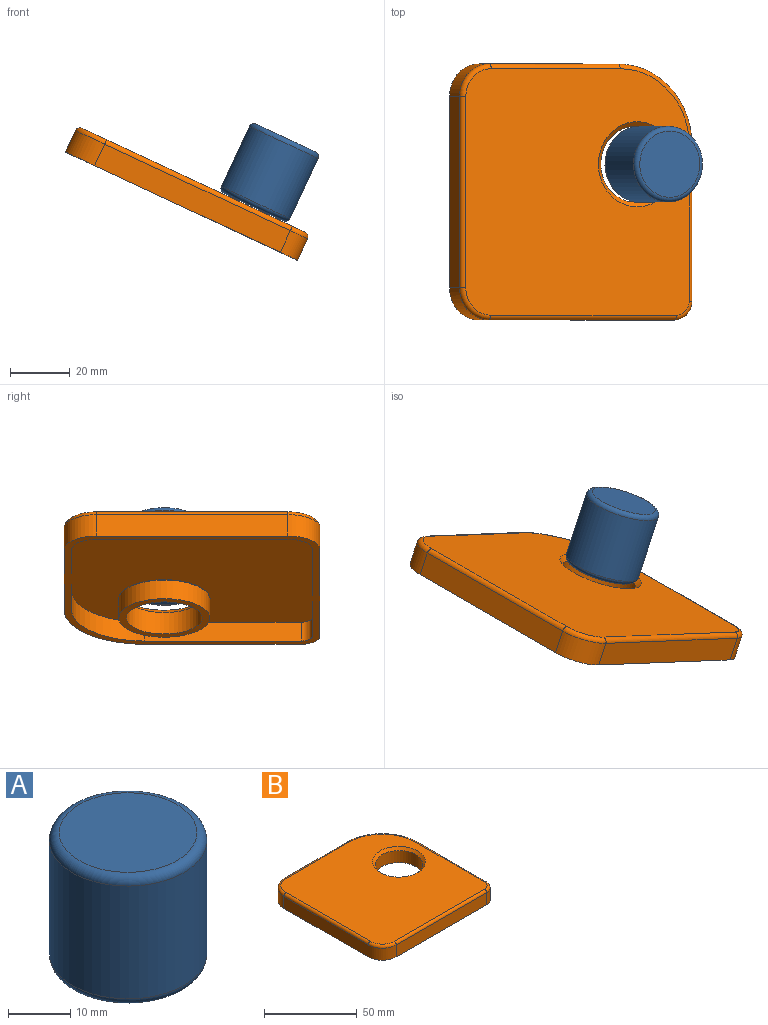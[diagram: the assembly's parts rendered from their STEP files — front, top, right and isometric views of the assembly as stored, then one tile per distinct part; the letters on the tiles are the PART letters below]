
ASSEMBLY  parts=2 mates=1
PART A: 5 faces, bbox 27.4x27.4x25.4 mm
  f0: cylinder r=12.67mm len=25.35mm, axis (0,0,-1), area 1769.9mm2, adj f3,f4
  f1: plane 22.17x22.17mm, normal (0,0,1), area 386.2mm2, adj f4
  f2: plane 22.17x22.17mm, normal (0,0,-1), area 386.2mm2, adj f3
  f3: torus R=11.09mm, axis (0,0,1), area 189.5mm2, adj f0,f2
  f4: torus R=11.09mm, axis (0,0,1), area 189.5mm2, adj f0,f1
PART B: 32 faces, bbox 88.9x88.8x9.5 mm
  f0: plane 30.48x30.48mm, normal (0,0,-1), area 223mm2, adj f11,f30
  f1: plane 85.73x85.73mm, normal (0,0,-1), area 790.6mm2, adj f2,f3,f4,f5,f6,f7,f8,f9
  f2: plane 47.71x7.94mm, normal (0,1,0), area 378.7mm2, adj f1,f3,f9,f14
  f3: cylinder r=10.94mm len=10.94mm, axis (0,0,-1), area 136.4mm2, adj f1,f2,f4,f16
  f4: plane 64.06x7.94mm, normal (-1,0,0), area 508.4mm2, adj f1,f3,f5,f18
  f5: cylinder r=10.73mm len=10.73mm, axis (0,0,-1), area 133.8mm2, adj f1,f4,f6,f20
  f6: plane 68.64x7.94mm, normal (0,-1,0), area 544.8mm2, adj f1,f5,f7,f19
  f7: cylinder r=6.35mm len=7.94mm, axis (0,0,-1), area 79.2mm2, adj f1,f6,f8,f17
  f8: plane 52.29x7.94mm, normal (1,0,0), area 415.1mm2, adj f1,f7,f9,f15
  f9: cylinder r=27.08mm len=27.08mm, axis (0,0,-1), area 337.7mm2, adj f1,f2,f8,f13
  f10: plane 82.55x82.55mm, normal (0,0,1), area 5992.1mm2, adj f12,f13,f14,f15,f16,f17,f18,f19
  f11: cylinder r=12.7mm len=25.4mm, axis (0,0,1), area 633.4mm2, adj f0,f12
  f12: cone r=12.7mm half-angle=45deg, axis (0,0,1), area 190.3mm2, adj f10,f11
  f13: torus R=25.5mm, axis (0,0,1), area 103.8mm2, adj f9,f10,f14,f15
  f14: cylinder r=1.59mm len=47.71mm, axis (1,0,0), area 119mm2, adj f2,f10,f13,f16
  f15: cylinder r=1.59mm len=52.29mm, axis (0,-1,0), area 130.4mm2, adj f8,f10,f13,f17
  f16: torus R=9.35mm, axis (0,0,1), area 40.6mm2, adj f3,f10,f14,f18
  f17: torus R=4.76mm, axis (0,0,1), area 22.6mm2, adj f7,f10,f15,f19
  f18: cylinder r=1.59mm len=64.06mm, axis (0,1,0), area 159.7mm2, adj f4,f10,f16,f20
  f19: cylinder r=1.59mm len=68.64mm, axis (-1,0,0), area 171.2mm2, adj f6,f10,f17,f20
  f20: torus R=9.15mm, axis (0,0,1), area 39.8mm2, adj f5,f10,f18,f19
  f21: plane 47.71x6.99mm, normal (0,-1,0), area 333.2mm2, adj f1,f22,f28,f29
  f22: cylinder r=8.4mm len=8.4mm, axis (0,0,-1), area 92.1mm2, adj f1,f21,f23,f29
  f23: plane 64.06x6.99mm, normal (1,0,0), area 447.4mm2, adj f1,f22,f24,f29
  f24: cylinder r=8.19mm len=8.19mm, axis (0,0,-1), area 89.9mm2, adj f1,f23,f25,f29
  f25: plane 68.64x6.99mm, normal (0,1,0), area 479.5mm2, adj f1,f24,f26,f29
  f26: cylinder r=3.81mm len=6.99mm, axis (0,0,-1), area 41.8mm2, adj f1,f25,f27,f29
  f27: plane 52.29x6.99mm, normal (-1,0,0), area 365.3mm2, adj f1,f26,f28,f29
  f28: cylinder r=24.54mm len=24.54mm, axis (0,0,-1), area 269.3mm2, adj f1,f21,f27,f29
  f29: plane 80.65x80.65mm, normal (0,0,-1), area 5602.5mm2, adj f21,f22,f23,f24,f25,f26,f27,f28
  f30: cylinder r=15.24mm len=30.48mm, axis (0,0,1), area 659.3mm2, adj f0,f31
  f31: cone r=14.5mm half-angle=45deg, axis (0,0,1), area 13.5mm2, adj f29,f30
PLACE A rot(axis=(0.21,0.21,0.95),92.7deg) t=(68,-34.24,-31.49)mm
PLACE B rot(axis=(0,1,0),25deg) t=(-16.34,-4.98,-3.2)mm fixed
MATE slider A.f0 <-> B.f11  axis (-0.42,0,-0.91) through (11.46,8.66,-3.37)mm
